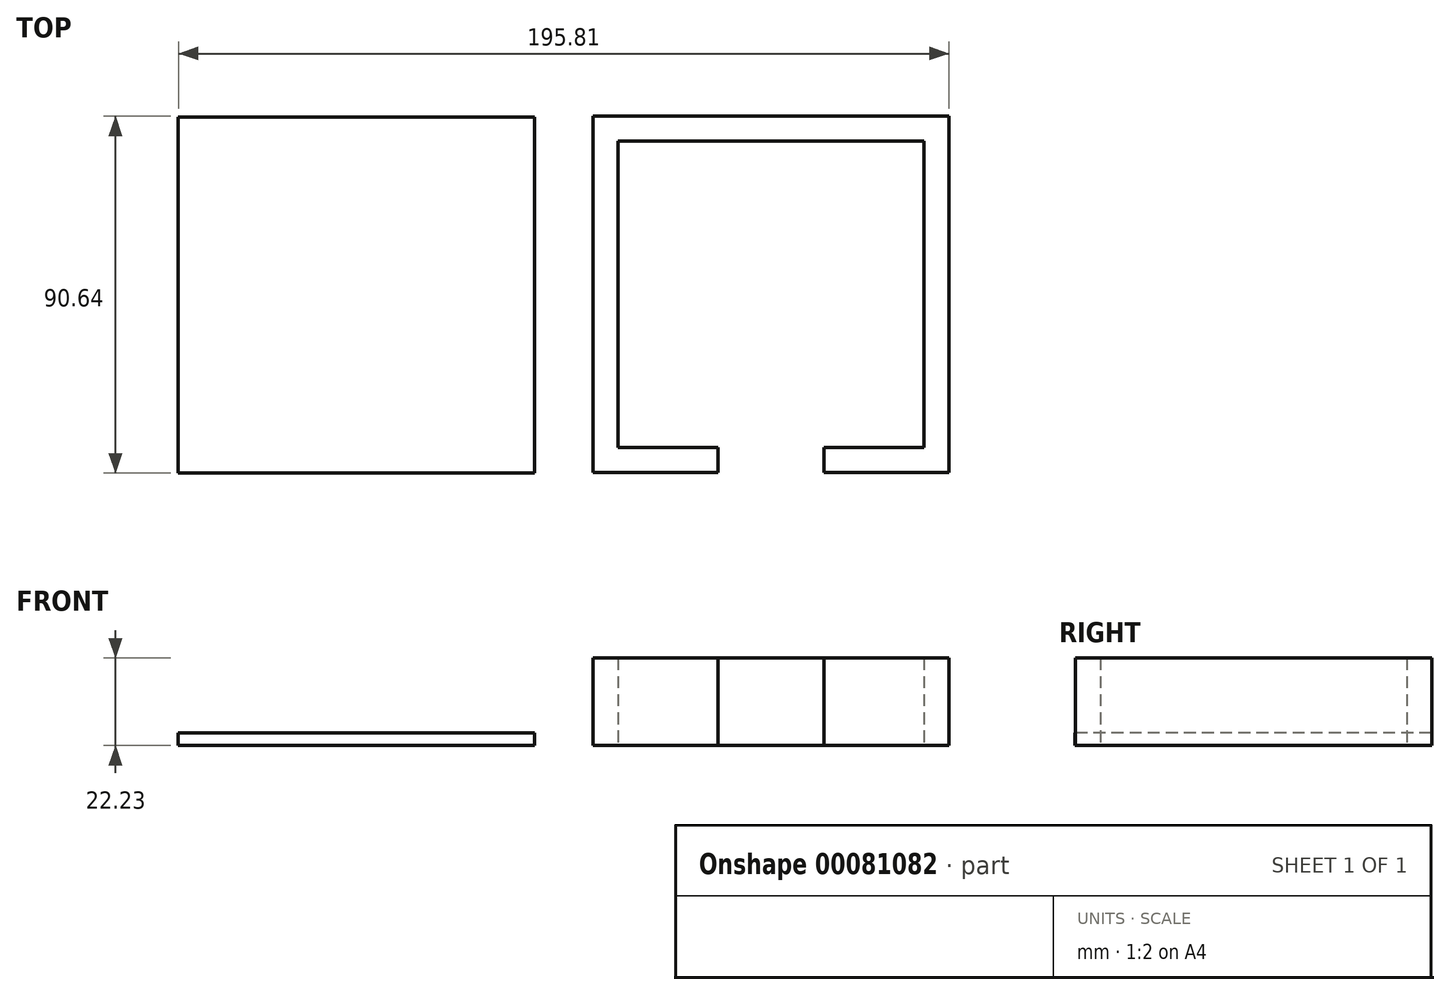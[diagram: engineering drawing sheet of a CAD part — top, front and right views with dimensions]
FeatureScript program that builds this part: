
annotation { "Feature Type Name" : "Feature", "Feature Type Description" : "" }
export const myFeature = defineFeature(function(context is Context, id is Id, definition is map)
    precondition{}
    {
        {
            var Q0;
            Q0=qCreatedBy(makeId("Top.planeOp"),FACE);
            var sketch = newSketch(context, id + "F0", { "sketchPlane" : qUnion([Q0])});
            skLineSegment(sketch, "E0.bottom", {"start": v(-45.3, 44.33) * mm, "end": v(45.2, 44.33) * mm});
            skLineSegment(sketch, "E0.top", {"start": v(-45.3, -46.16) * mm, "end": v(45.2, -46.16) * mm});
            skLineSegment(sketch, "E0.left", {"start": v(-45.3, 44.33) * mm, "end": v(-45.3, -46.16) * mm});
            skLineSegment(sketch, "E0.right", {"start": v(45.2, 44.33) * mm, "end": v(45.2, -46.16) * mm});
            skLineSegment(sketch, "E1.bottom", {"start": v(-38.94, 37.98) * mm, "end": v(38.85, 37.98) * mm});
            skLineSegment(sketch, "E1.top", {"start": v(-38.94, -39.8) * mm, "end": v(38.85, -39.8) * mm});
            skLineSegment(sketch, "E1.left", {"start": v(-38.94, 37.98) * mm, "end": v(-38.94, -39.8) * mm});
            skLineSegment(sketch, "E1.right", {"start": v(38.85, 37.98) * mm, "end": v(38.85, -39.8) * mm});
            skLineSegment(sketch, "E2.bottom", {"start": v(-13.54, -39.8) * mm, "end": v(13.45, -39.8) * mm});
            skLineSegment(sketch, "E2.top", {"start": v(-13.54, -46.16) * mm, "end": v(13.45, -46.16) * mm});
            skLineSegment(sketch, "E2.left", {"start": v(-13.54, -39.8) * mm, "end": v(-13.54, -46.16) * mm});
            skLineSegment(sketch, "E2.right", {"start": v(13.45, -39.8) * mm, "end": v(13.45, -46.16) * mm});
            skLineSegment(sketch, "E3.bottom", {"start": v(-150.61, 44.17) * mm, "end": v(-60.13, 44.17) * mm});
            skLineSegment(sketch, "E3.top", {"start": v(-150.61, -46.31) * mm, "end": v(-60.13, -46.31) * mm});
            skLineSegment(sketch, "E3.left", {"start": v(-150.61, 44.17) * mm, "end": v(-150.61, -46.31) * mm});
            skLineSegment(sketch, "E3.right", {"start": v(-60.13, 44.17) * mm, "end": v(-60.13, -46.31) * mm});
            skSolve(sketch);
        }
        {
            var Q0;
            Q0=makeQuery(id+"F0.imprint","IMPRINT",FACE,{"disambiguationData":[TD([[makeQuery(id+"F0.imprint","IMPRINT",EDGE,{"derivedFrom":sQuery(id+"F0.wireOp",EDGE,"E3.bottom")}),-1.0]])]});
            extrude(context, id + "F1", {"entities" : qUnion([Q0]), "depth" : 3.17 * mm});
        }
        {
            var Q0;
            Q0=makeQuery(id+"F0.imprint","IMPRINT",FACE,{"disambiguationData":[TD([[makeQuery(id+"F0.imprint","IMPRINT",EDGE,{"derivedFrom":sQuery(id+"F0.wireOp",EDGE,"E0.bottom")}),-1.0]])]});
            extrude(context, id + "F2", {"entities" : qUnion([Q0]), "depth" : 22.22 * mm});
        }
    });
